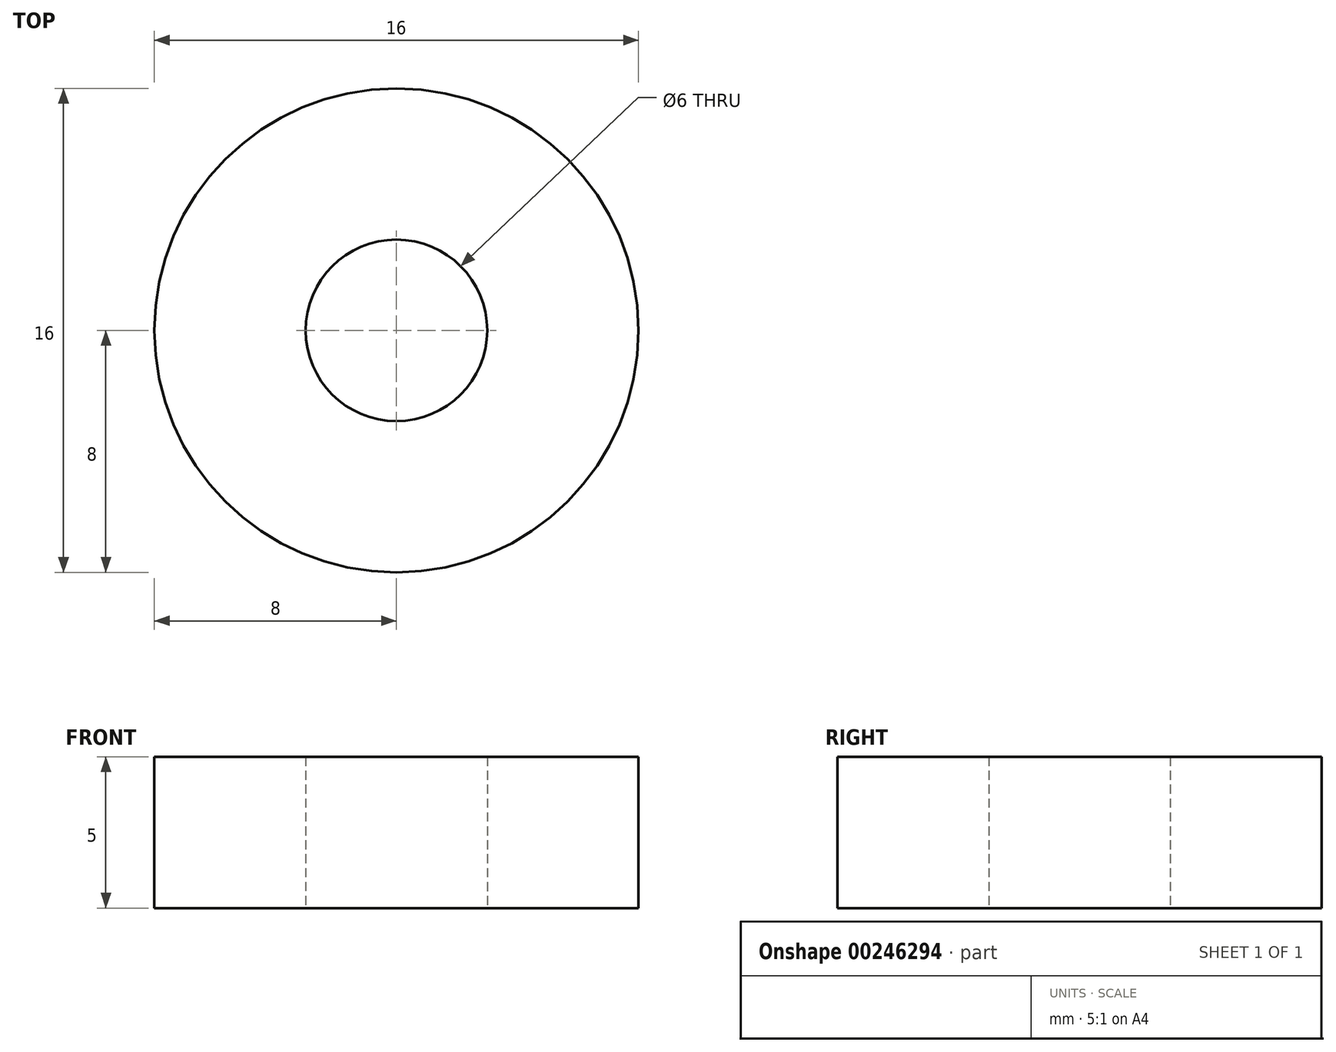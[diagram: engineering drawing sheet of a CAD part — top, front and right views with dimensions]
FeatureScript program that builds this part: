
annotation { "Feature Type Name" : "Feature", "Feature Type Description" : "" }
export const myFeature = defineFeature(function(context is Context, id is Id, definition is map)
    precondition{}
    {
        {
            var Q0;
            Q0=qCreatedBy(makeId("Top.planeOp"),FACE);
            var sketch = newSketch(context, id + "F0", { "sketchPlane" : qUnion([Q0])});
            skCircle(sketch, "E0", {"center": v(0, 0) * mm, "radius": 3 * mm});
            skCircle(sketch, "E1", {"center": v(0, 0) * mm, "radius": 8 * mm});
            skSolve(sketch);
        }
        {
            var Q0;
            Q0 = qSketchRegion(id + "F0", true);
            extrude(context, id + "F1", {"entities" : qUnion([Q0]), "depth" : 5 * mm});
        }
    });
